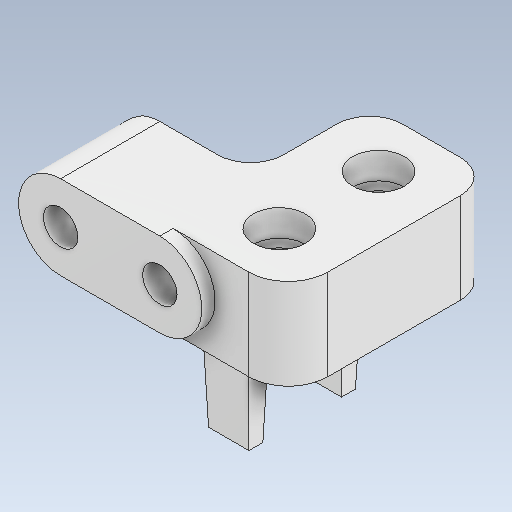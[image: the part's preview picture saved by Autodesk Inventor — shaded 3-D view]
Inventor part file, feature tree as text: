
AUTODESK INVENTOR PART (.ipt)
format: ipt  version: 2021 (Build 250183000, 183)  size: 287,232 bytes
history: native  units: mm
features: extrude x8, sketch x6, projected_geometry x6, fillet x2, other x1
ambient origin geometry x8: Origin, YZ Plane, XZ Plane, XY Plane, X Axis, Y Axis, Z Axis, Center Point
bodies: Body1 (feature_tree)
feature tree (23):
  other  "솔리드1"
  sketch  "스케치1"
  extrude  "돌출1"  Depth=18.7mm
  extrude  "돌출2"  Depth=2.8mm
  extrude  "돌출3"  Depth=6.8mm
  extrude  "돌출4"  Depth=10.0mm
  extrude  "돌출5"  Depth=15.0mm
  extrude  "돌출6"  Depth=4.2mm
  fillet  "모깎기1"  Radius=8.0mm
  sketch  "스케치7"
  extrude  "돌출8"  Depth=15.0mm
  extrude  "돌출9"  Depth=12.7mm
  fillet  "모깎기2"  Radius=80.0mm
  sketch  "스케치2"
  projected_geometry  "투영된 루프1"
  sketch  "스케치3"
  projected_geometry  "투영된 루프2"
  sketch  "스케치4"
  projected_geometry  "투영된 루프3"
  sketch  "스케치5"
  projected_geometry  "투영된 루프4"
  projected_geometry  "투영된 루프5"
  projected_geometry  "투영된 루프6"
